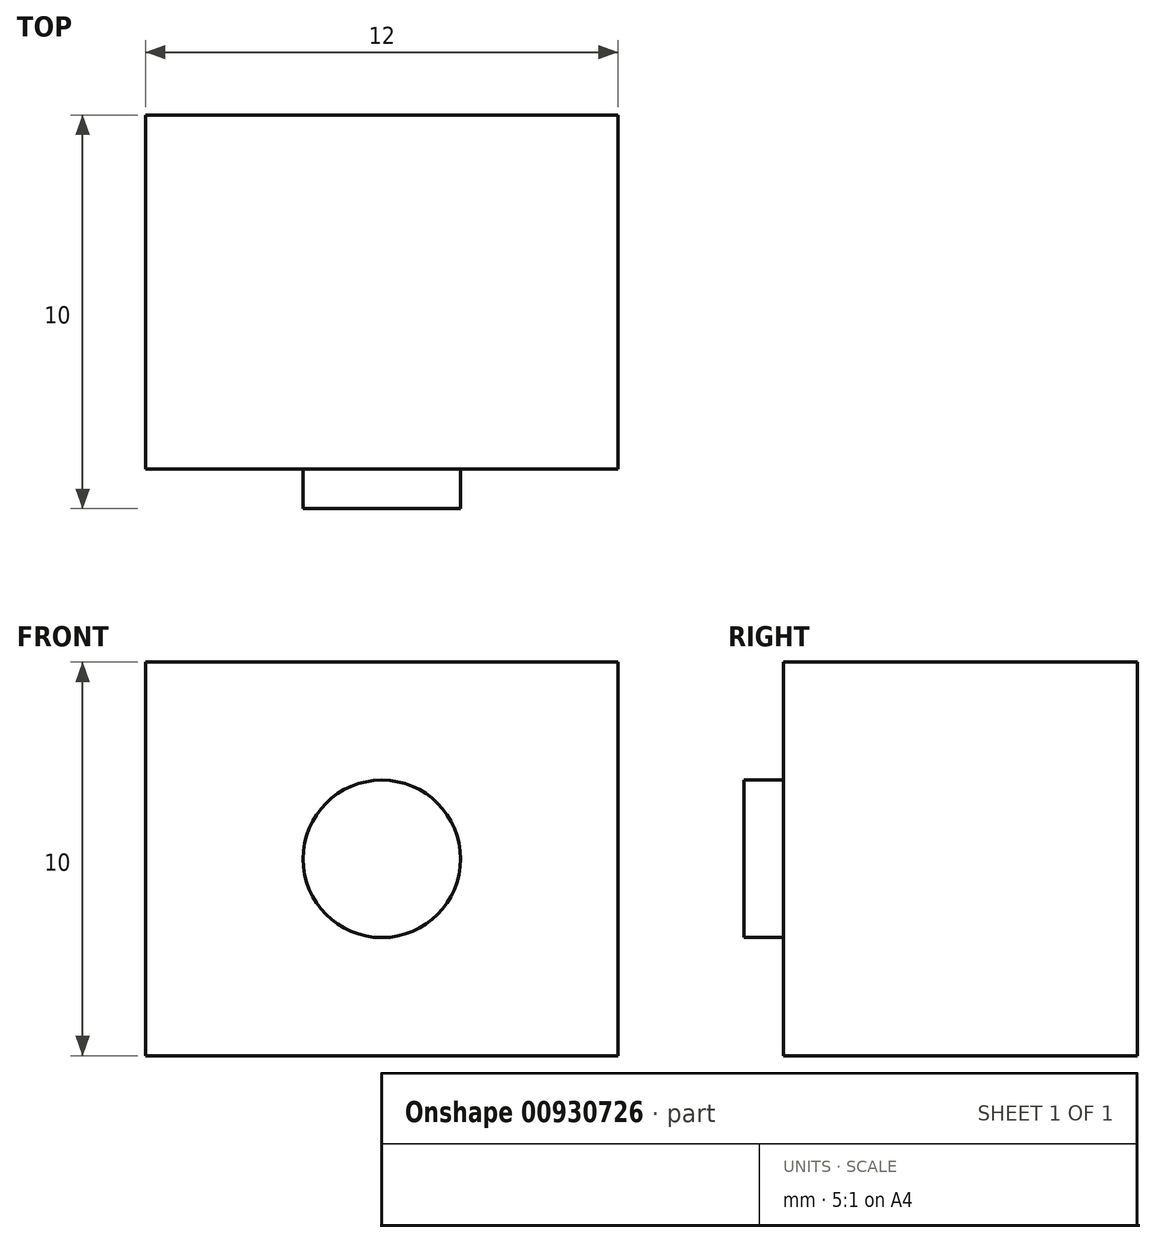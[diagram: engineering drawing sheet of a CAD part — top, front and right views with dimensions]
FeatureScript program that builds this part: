
annotation { "Feature Type Name" : "Feature", "Feature Type Description" : "" }
export const myFeature = defineFeature(function(context is Context, id is Id, definition is map)
    precondition{}
    {
        {
            var Q0;
            Q0=qCreatedBy(makeId("Front.planeOp"),FACE);
            var sketch = newSketch(context, id + "F0", { "sketchPlane" : qUnion([Q0])});
            skLineSegment(sketch, "E0.bottom", {"start": v(0, 0) * mm, "end": v(12, 0) * mm});
            skLineSegment(sketch, "E0.top", {"start": v(0, 10) * mm, "end": v(12, 10) * mm});
            skLineSegment(sketch, "E0.left", {"start": v(0, 0) * mm, "end": v(0, 10) * mm});
            skLineSegment(sketch, "E0.right", {"start": v(12, 0) * mm, "end": v(12, 10) * mm});
            skCircle(sketch, "E1", {"center": v(6, 5) * mm, "radius": 2 * mm});
            skPoint(sketch, "E1.centerSnap0", {"position": v(12, 5) * mm});
            skPoint(sketch, "E1.centerSnap1", {"position": v(6, 0) * mm});
            skSolve(sketch);
        }
        {
            var Q0;
            Q0=makeQuery(id+"F0.imprint","IMPRINT",FACE,{"disambiguationData":[TD([[makeQuery(id+"F0.imprint","IMPRINT",EDGE,{"derivedFrom":sQuery(id+"F0.wireOp",EDGE,"E0.bottom")}),1.0]])]});
            var Q1;
            Q1=makeQuery(id+"F0.imprint","IMPRINT",FACE,{"disambiguationData":[TD([[makeQuery(id+"F0.imprint","IMPRINT",EDGE,{"derivedFrom":sQuery(id+"F0.wireOp",EDGE,"E1")}),1.0]])]});
            extrude(context, id + "F1", {"entities" : qUnion([Q0, Q1]), "oppositeDirection" : true, "depth" : 9 * mm, "offsetDistance" : 25 * mm});
        }
        {
            var Q0;
            Q0=makeQuery(id+"F0.imprint","IMPRINT",FACE,{"disambiguationData":[TD([[makeQuery(id+"F0.imprint","IMPRINT",EDGE,{"derivedFrom":sQuery(id+"F0.wireOp",EDGE,"E1")}),1.0]])]});
            extrude(context, id + "F2", {"entities" : qUnion([Q0]), "operationType" : NewBodyOperationType.ADD, "depth" : 1 * mm, "offsetDistance" : 25 * mm});
        }
    });
